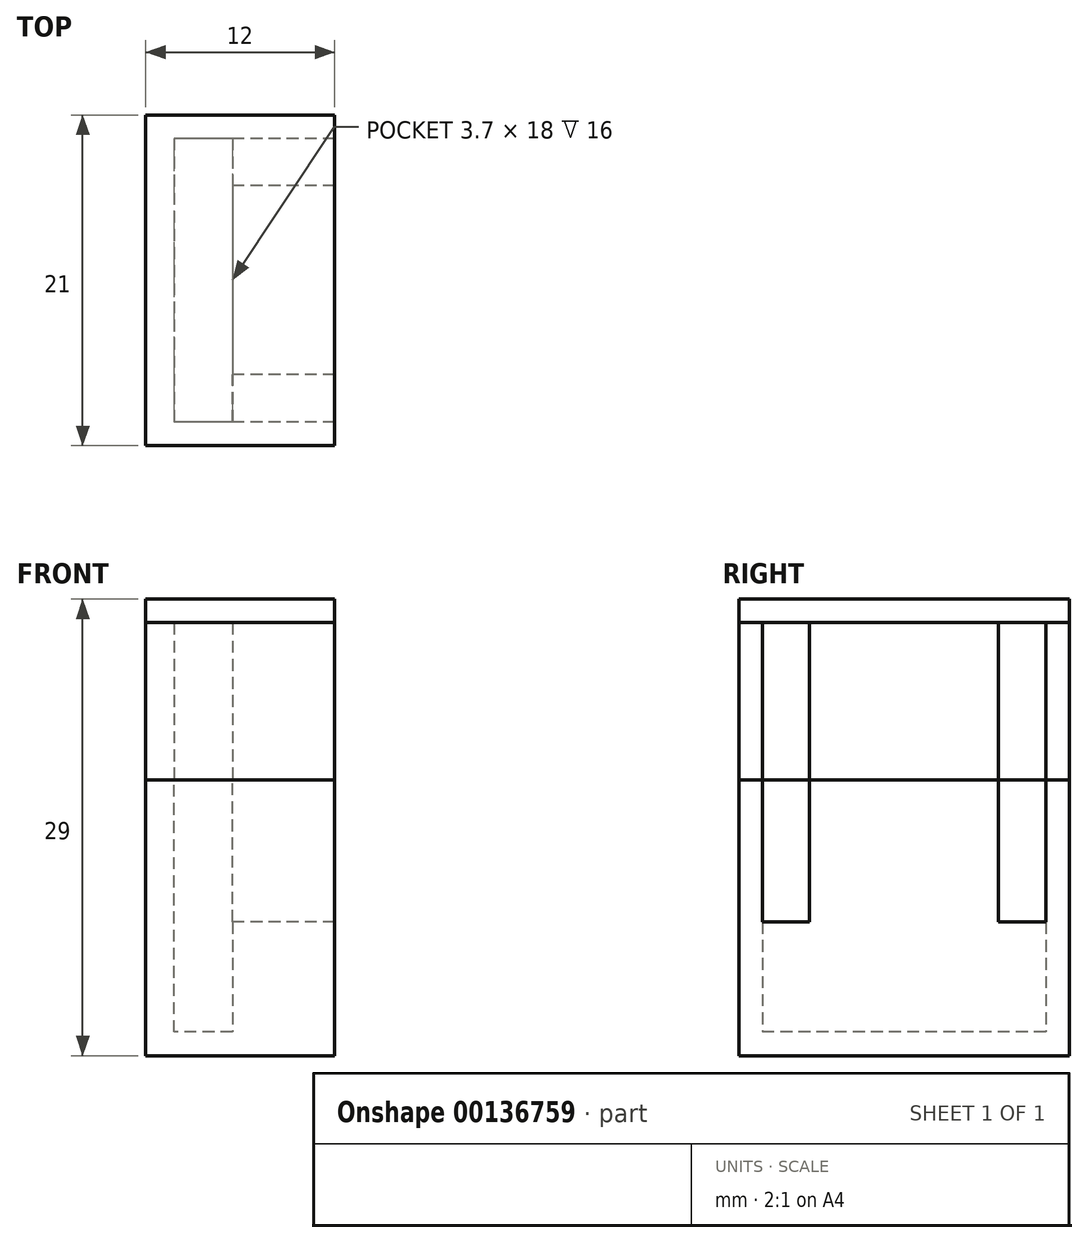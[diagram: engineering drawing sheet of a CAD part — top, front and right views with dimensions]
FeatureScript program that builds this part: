
annotation { "Feature Type Name" : "Feature", "Feature Type Description" : "" }
export const myFeature = defineFeature(function(context is Context, id is Id, definition is map)
    precondition{}
    {
        {
            var Q0;
            Q0=qCreatedBy(makeId("Top.planeOp"),FACE);
            var sketch = newSketch(context, id + "F0", { "sketchPlane" : qUnion([Q0])});
            skLineSegment(sketch, "E0.bottom", {"start": v(-5.6, 4.56) * mm, "end": v(-12.1, 4.56) * mm});
            skLineSegment(sketch, "E0.top", {"start": v(-5.6, -7.44) * mm, "end": v(-12.1, -7.44) * mm});
            skLineSegment(sketch, "E0.left", {"start": v(-5.6, 4.56) * mm, "end": v(-5.6, -7.44) * mm});
            skLineSegment(sketch, "E0.right", {"start": v(-12.1, 4.56) * mm, "end": v(-12.1, -7.44) * mm});
            skLineSegment(sketch, "E1", {"start": v(-17.6, 9.06) * mm, "end": v(-23.16, 10.18) * mm});
            skLineSegment(sketch, "E2", {"start": v(-5.6, -11.94) * mm, "end": v(1.55, -11.94) * mm});
            skLineSegment(sketch, "E3.bottom", {"start": v(-17.6, 9.06) * mm, "end": v(-5.6, 9.06) * mm});
            skLineSegment(sketch, "E3.top", {"start": v(-17.6, -11.94) * mm, "end": v(-5.6, -11.94) * mm});
            skLineSegment(sketch, "E3.left", {"start": v(-17.6, 9.06) * mm, "end": v(-17.6, -11.94) * mm});
            skLineSegment(sketch, "E3.right", {"start": v(-5.6, 9.06) * mm, "end": v(-5.6, 7.56) * mm});
            skLineSegment(sketch, "E4.0", {"start": v(-15.8, 7.56) * mm, "end": v(-15.8, -10.44) * mm});
            skLineSegment(sketch, "E5.0", {"start": v(-5.6, 7.56) * mm, "end": v(-15.8, 7.56) * mm});
            skLineSegment(sketch, "E6.0", {"start": v(-5.6, -10.44) * mm, "end": v(-15.8, -10.44) * mm});
            skLineSegment(sketch, "E7", {"start": v(-5.6, -10.44) * mm, "end": v(-5.6, -11.94) * mm});
            skSolve(sketch);
        }
        {
            var Q0;
            Q0=makeQuery(id+"F0.imprint","IMPRINT",FACE,{"disambiguationData":[TD([[makeQuery(id+"F0.imprint","IMPRINT",EDGE,{"derivedFrom":sQuery(id+"F0.wireOp",EDGE,"E3.bottom")}),-1.0]])]});
            var Q1;
            Q1=makeQuery(id+"F0.imprint","IMPRINT",FACE,{"disambiguationData":[TD([[makeQuery(id+"F0.imprint","IMPRINT",EDGE,{"derivedFrom":sQuery(id+"F0.wireOp",EDGE,"E0.bottom")}),1.0]])]});
            var Q2;
            Q2 = qSketchRegion(id + "Fzzpuh2WvLhzNMt_2", true);
            extrude(context, id + "F1", {"entities" : qUnion([Q0, Q1, Q2]), "depth" : 10 * mm});
        }
        {
            var Q0;
            Q0=makeQuery(id+"F1.opExtrude","CAP_FACE",FACE,{"disambiguationData":[OSD([sQuery(id+"F0.wireOp",EDGE,"E3.bottom"),sQuery(id+"F0.wireOp",EDGE,"E3.top"),sQuery(id+"F0.wireOp",EDGE,"E3.left"),sQuery(id+"F0.wireOp",EDGE,"E3.right"),sQuery(id+"F0.wireOp",EDGE,"E4.0"),sQuery(id+"F0.wireOp",EDGE,"E5.0"),sQuery(id+"F0.wireOp",EDGE,"E6.0"),sQuery(id+"F0.wireOp",EDGE,"E7")])],"isStart":false});
            var sketch = newSketch(context, id + "F2", { "sketchPlane" : qUnion([Q0])});
            skLineSegment(sketch, "E8.bottom", {"start": v(-17.6, 9.06) * mm, "end": v(-5.6, 9.06) * mm});
            skLineSegment(sketch, "E8.top", {"start": v(-17.6, -11.94) * mm, "end": v(-5.6, -11.94) * mm});
            skLineSegment(sketch, "E8.left", {"start": v(-17.6, 9.06) * mm, "end": v(-17.6, -11.94) * mm});
            skLineSegment(sketch, "E8.right", {"start": v(-5.6, 9.06) * mm, "end": v(-5.6, -11.94) * mm});
            skSolve(sketch);
        }
        {
            var Q0;
            {var subQ1=sQuery(id+"F2.wireOp",EDGE,"E8.bottom");Q0=makeQuery(id+"F2.imprint","IMPRINT",FACE,{"disambiguationData":[TD([[makeQuery(id+"F2.imprint","IMPRINT",EDGE,{"derivedFrom":subQ1}),-1.0]])]});}
            var Q1;
            Q1=makeQuery(id+"F2.imprint","IMPRINT",FACE,{"disambiguationData":[TD([[makeQuery(id+"F2.imprint","IMPRINT",EDGE,{"derivedFrom":makeQuery(id+"F1.opExtrude","CAP_EDGE",EDGE,{"disambiguationData":[OSD([sQuery(id+"F0.wireOp",EDGE,"E4.0")])],"isStart":false})}),1.0]])]});
            extrude(context, id + "F3", {"entities" : qUnion([Q0, Q1]), "depth" : 1.5 * mm});
        }
        {
            var Q0;
            Q0=makeQuery(id+"F0.imprint","IMPRINT",FACE,{"disambiguationData":[TD([[makeQuery(id+"F0.imprint","IMPRINT",EDGE,{"derivedFrom":sQuery(id+"F0.wireOp",EDGE,"E3.bottom")}),-1.0]])]});
            var Q1;
            Q1=makeQuery(id+"F0.imprint","IMPRINT",FACE,{"disambiguationData":[TD([[makeQuery(id+"F0.imprint","IMPRINT",EDGE,{"derivedFrom":sQuery(id+"F0.wireOp",EDGE,"E0.bottom")}),1.0]])]});
            extrude(context, id + "F4", {"entities" : qUnion([Q0, Q1]), "oppositeDirection" : true, "depth" : 16 * mm});
        }
        {
            var Q0;
            Q0=makeQuery(id+"F4.opExtrude","CAP_FACE",FACE,{"disambiguationData":[OSD([sQuery(id+"F0.wireOp",EDGE,"E3.bottom"),sQuery(id+"F0.wireOp",EDGE,"E3.top"),sQuery(id+"F0.wireOp",EDGE,"E3.left"),sQuery(id+"F0.wireOp",EDGE,"E3.right"),sQuery(id+"F0.wireOp",EDGE,"E4.0"),sQuery(id+"F0.wireOp",EDGE,"E5.0"),sQuery(id+"F0.wireOp",EDGE,"E6.0"),sQuery(id+"F0.wireOp",EDGE,"E7")])],"isStart":false});
            var sketch = newSketch(context, id + "F5", { "sketchPlane" : qUnion([Q0])});
            skLineSegment(sketch, "E9.bottom", {"start": v(-17.6, 11.94) * mm, "end": v(-5.6, 11.94) * mm});
            skLineSegment(sketch, "E9.top", {"start": v(-17.6, -9.06) * mm, "end": v(-5.6, -9.06) * mm});
            skLineSegment(sketch, "E9.left", {"start": v(-17.6, 11.94) * mm, "end": v(-17.6, -9.06) * mm});
            skLineSegment(sketch, "E9.right", {"start": v(-5.6, 11.94) * mm, "end": v(-5.6, -9.06) * mm});
            skLineSegment(sketch, "E10.bottom", {"start": v(-5.6, 10.44) * mm, "end": v(-12.1, 10.44) * mm});
            skLineSegment(sketch, "E10.top", {"start": v(-5.6, 7.44) * mm, "end": v(-12.1, 7.44) * mm});
            skLineSegment(sketch, "E10.left", {"start": v(-5.6, 10.44) * mm, "end": v(-5.6, 7.44) * mm});
            skLineSegment(sketch, "E10.right", {"start": v(-12.1, 10.44) * mm, "end": v(-12.1, 7.44) * mm});
            skLineSegment(sketch, "E11.bottom", {"start": v(-5.6, -7.56) * mm, "end": v(-12.1, -7.56) * mm});
            skLineSegment(sketch, "E11.top", {"start": v(-5.6, -4.56) * mm, "end": v(-12.1, -4.56) * mm});
            skLineSegment(sketch, "E11.left", {"start": v(-5.6, -7.56) * mm, "end": v(-5.6, -4.56) * mm});
            skLineSegment(sketch, "E11.right", {"start": v(-12.1, -7.56) * mm, "end": v(-12.1, -4.56) * mm});
            skSolve(sketch);
        }
        {
            var Q0;
            {var subQ3=sQuery(id+"F5.wireOp",EDGE,"E9.bottom");Q0=makeQuery(id+"F5.imprint","IMPRINT",FACE,{"disambiguationData":[TD([[makeQuery(id+"F5.imprint","IMPRINT",EDGE,{"derivedFrom":subQ3}),-1.0]])]});}
            var Q1;
            Q1=makeQuery(id+"F5.imprint","IMPRINT",FACE,{"disambiguationData":[TD([[makeQuery(id+"F5.imprint","IMPRINT",EDGE,{"derivedFrom":makeQuery(id+"F4.opExtrude","CAP_EDGE",EDGE,{"disambiguationData":[OSD([sQuery(id+"F0.wireOp",EDGE,"E4.0")])],"isStart":false})}),-1.0]])]});
            extrude(context, id + "F6", {"entities" : qUnion([Q0, Q1]), "depth" : 1.5 * mm});
        }
        {
            var Q0;
            Q0=makeQuery(id+"F5.imprint","IMPRINT",FACE,{"disambiguationData":[TD([[makeQuery(id+"F5.imprint","IMPRINT",EDGE,{"derivedFrom":sQuery(id+"F5.wireOp",EDGE,"E11.bottom")}),-1.0]])]});
            var Q1;
            Q1=makeQuery(id+"F5.imprint","IMPRINT",FACE,{"disambiguationData":[TD([[makeQuery(id+"F5.imprint","IMPRINT",EDGE,{"derivedFrom":sQuery(id+"F5.wireOp",EDGE,"E10.bottom")}),1.0]])]});
            extrude(context, id + "F7", {"entities" : qUnion([Q0, Q1]), "operationType" : NewBodyOperationType.ADD, "depth" : 1.5 * mm});
        }
        {
            var Q0;
            Q0=makeQuery(id+"F5.imprint","IMPRINT",FACE,{"disambiguationData":[TD([[makeQuery(id+"F5.imprint","IMPRINT",EDGE,{"derivedFrom":sQuery(id+"F5.wireOp",EDGE,"E11.bottom")}),-1.0]])]});
            var Q1;
            Q1=makeQuery(id+"F5.imprint","IMPRINT",FACE,{"disambiguationData":[TD([[makeQuery(id+"F5.imprint","IMPRINT",EDGE,{"derivedFrom":sQuery(id+"F5.wireOp",EDGE,"E10.bottom")}),1.0]])]});
            extrude(context, id + "F8", {"entities" : qUnion([Q0, Q1]), "operationType" : NewBodyOperationType.ADD, "oppositeDirection" : true, "depth" : 7 * mm});
        }
    });
